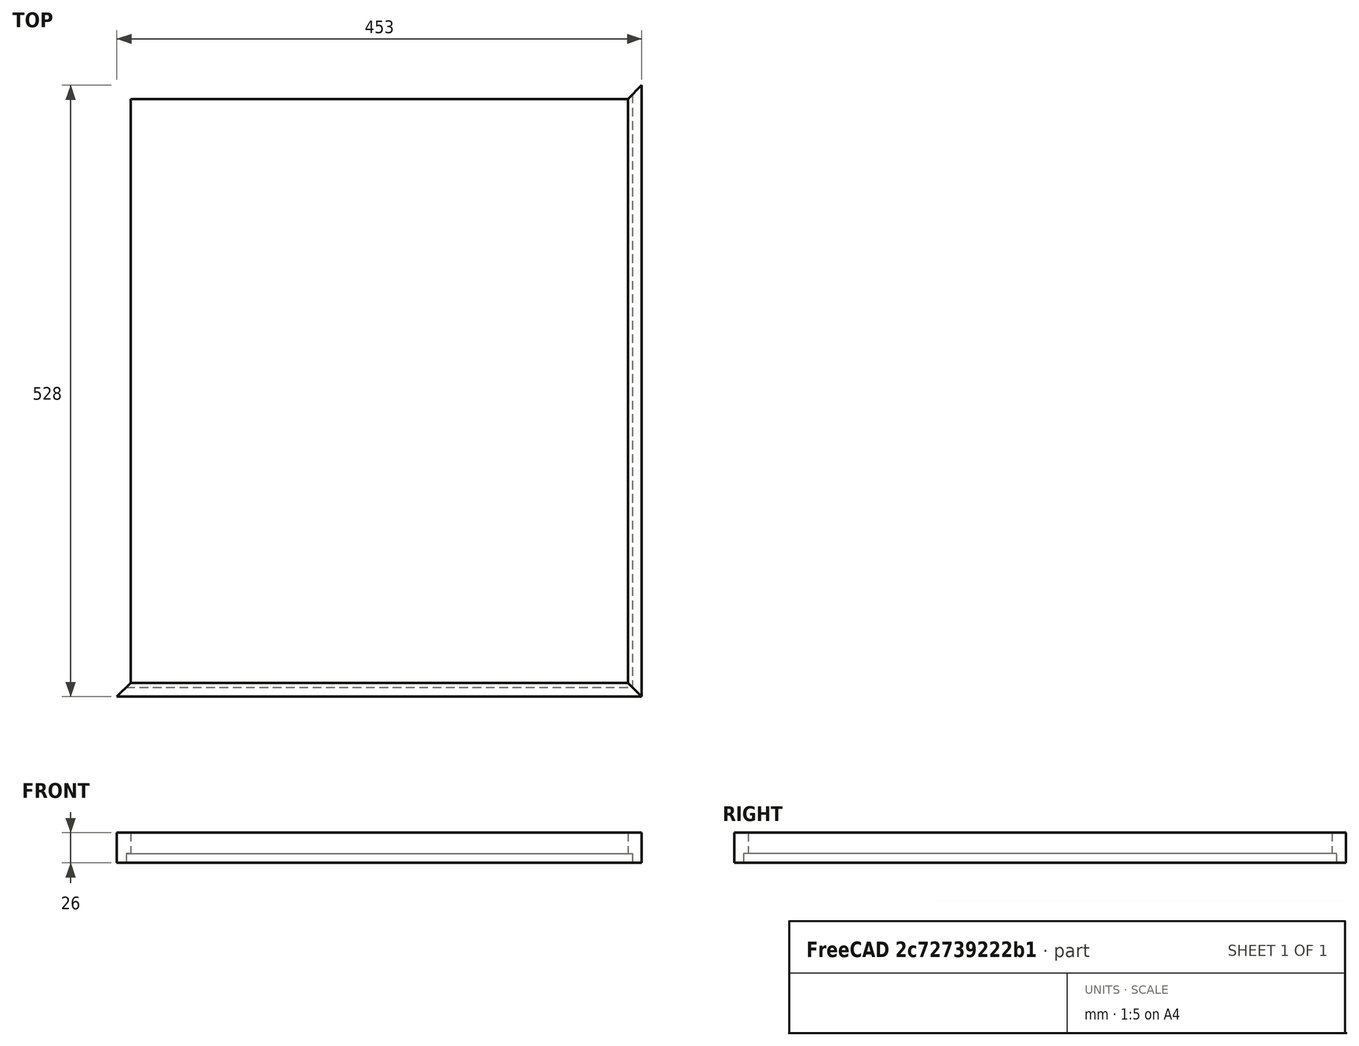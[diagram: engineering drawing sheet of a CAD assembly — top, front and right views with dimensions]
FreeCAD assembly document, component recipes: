
FREECAD ASSEMBLY — COMPONENT RECIPES ("streha")

This assembly document has 3 components, labeled P0..P2 below (a component is one placed body or linked part). 3 of them carry a construction recipe — the FreeCAD feature program that regenerates the part from scratch, quoted from this document or its linked companion documents; the rest are supplied as boundary geometry only. No exploded tour is included for this assembly.
COMPONENT P0 — recipe-attached ("slat_side", modeled in this document).
Construction recipe (the document's own serialized feature program — sketch geometry with constraints, then the solid features built on it; lengths are millimeters unless a unit is written):

FEATURE [PartDesign::CoordinateSystem] LCS_0005
  AttacherType = Attacher::AttachEngine3D
  MapMode = 2
  Support = -> [X_Axis006]
FEATURE [Sketcher::SketchObject] Sketch003  label="Sketch004"
  FullyConstrained = true
  MapMode = 5
  Placement = pos=(0,0,0) rot=(1,0,0;1.5708rad)
  Support = -> [XZ_Plane006]
  expr: Constraints[12] = Variables.inner_width / 2 + Variables.wall_thickness
  sketch-geometry (6):
    g0: LineSegment StartX=214.5 StartY=0 StartZ=0 EndX=218.5 EndY=0 EndZ=0
    g1: LineSegment StartX=218.5 StartY=0 StartZ=0 EndX=218.5 EndY=-8 EndZ=0
    g2: LineSegment StartX=218.5 StartY=-8 StartZ=0 EndX=226.5 EndY=-8 EndZ=0
    g3: LineSegment StartX=226.5 StartY=-8 StartZ=0 EndX=226.5 EndY=25.6324 EndZ=0
    g4: LineSegment StartX=214.5 StartY=30 StartZ=0 EndX=214.5 EndY=0 EndZ=0
    g5: LineSegment StartX=214.5 StartY=30 StartZ=0 EndX=226.5 EndY=25.6324 EndZ=0
  constraints (18):
    c: Horizontal(g0)
    c: Coincident(g0,g1)
    c: Vertical(g1)
    c: Coincident(g1,g2)
    c: Horizontal(g2)
    c: Coincident(g2,g3)
    c: Vertical(g3)
    c: Coincident(g4,g0)
    c: Vertical(g4)
    c: DistanceX(g0,g0) = 4  'c'
    c: DistanceY(g1,g1) = 8  'd'
    c: Horizontal(g0,g-1)
    c: DistanceX(g-1,g0) = 214.5
    c: DistanceX(g0,g2) = 12  'a'
    c: DistanceY(g4,g4) = 30  'b'
    c: Coincident(g5,g4)
    c: Coincident(g5,g3)
    c: Angle(g5) = -0.349066  'e'
FEATURE [PartDesign::Pad] Pad002
  Direction = (1,1,1)
  Length = 700
  Length2 = 100
  Midplane = true
  Placement = pos=(0,0,0) rot=(1,0,0;1.5708rad)
  Profile = -> Sketch003
  Type = 0
FEATURE [Sketcher::SketchObject] Sketch004  label="Sketch005"
  ExternalGeometry = -> [Pad002]
  FullyConstrained = true
  MapMode = 5
  Support = -> [XY_Plane006]
  expr: Constraints[14] = Variables.inner_depth + 2 * Variables.wall_thickness
  sketch-geometry (8):
    g0: LineSegment StartX=226.5 StartY=-350 StartZ=0 EndX=226.5 EndY=-264 EndZ=0
    g1: LineSegment StartX=226.5 StartY=-264 StartZ=0 EndX=214.5 EndY=-252 EndZ=0
    g2: LineSegment StartX=214.5 StartY=-252 StartZ=0 EndX=214.5 EndY=-350 EndZ=0
    g3: LineSegment StartX=226.5 StartY=350 StartZ=0 EndX=226.5 EndY=264 EndZ=0
    g4: LineSegment StartX=226.5 StartY=264 StartZ=0 EndX=214.5 EndY=252 EndZ=0
    g5: LineSegment StartX=214.5 StartY=252 StartZ=0 EndX=214.5 EndY=350 EndZ=0
    g6: LineSegment StartX=214.5 StartY=-350 StartZ=0 EndX=226.5 EndY=-350 EndZ=0
    g7: LineSegment StartX=214.5 StartY=350 StartZ=0 EndX=226.5 EndY=350 EndZ=0
  constraints (20):
    c: Coincident(g0,g-4)
    c: Coincident(g1,g0)
    c: Coincident(g2,g1)
    c: Coincident(g2,g-4)
    c: Vertical(g2)
    c: Vertical(g0)
    c: Coincident(g-3,g3)
    c: Vertical(g3)
    c: Coincident(g3,g4)
    c: Coincident(g4,g5)
    c: Coincident(g5,g-3)
    c: Vertical(g5)
    c: Equal(g4,g1)
    c: Equal(g5,g2)
    c: DistanceY(g1,g4) = 504
    c: Coincident(g6,g2)
    c: Coincident(g6,g0)
    c: Coincident(g7,g5)
    c: Coincident(g7,g3)
    c: Perpendicular(g4,g1)
FEATURE [PartDesign::Pocket] Pocket001
  BaseFeature = -> Pad002
  Length = 41
  Length2 = 100
  Midplane = true
  Placement = pos=(0,0,0) rot=(1,0,0;1.5708rad)
  Profile = -> Sketch004
  Type = 1
FEATURE [Sketcher::SketchObject] Sketch
  ExternalGeometry = -> [Pocket001]
  FullyConstrained = true
  MapMode = 5
  Placement = pos=(0,0,0) rot=(1,0,0;1.5708rad)
  Support = -> [XZ_Plane006]
  expr: Constraints[10] = Variables.bottom_thickness
  sketch-geometry (4):
    g0: LineSegment StartX=214.5 StartY=18 StartZ=0 EndX=226.5 EndY=18 EndZ=0
    g1: LineSegment StartX=226.5 StartY=18 StartZ=0 EndX=226.5 EndY=30 EndZ=0
    g2: LineSegment StartX=226.5 StartY=30 StartZ=0 EndX=214.5 EndY=30 EndZ=0
    g3: LineSegment StartX=214.5 StartY=30 StartZ=0 EndX=214.5 EndY=18 EndZ=0
  constraints (11):
    c: Coincident(g0,g1)
    c: Coincident(g1,g2)
    c: Coincident(g2,g3)
    c: Coincident(g3,g0)
    c: Horizontal(g0)
    c: Horizontal(g2)
    c: Vertical(g1)
    c: Vertical(g3)
    c: Coincident(g2,g-3)
    c: PointOnObject(g-3,g1)
    c: DistanceY(g-1,g0) = 18
FEATURE [PartDesign::Pocket] Pocket
  BaseFeature = -> Pocket001
  Length = 5
  Length2 = 100
  Midplane = true
  Placement = pos=(0,0,0) rot=(1,0,0;1.5708rad)
  Profile = -> Sketch
  Type = 1
FEATURE [PartDesign::Body] Body_3
  Group = -> [LCS_0005,Sketch003,Pad002,Sketch004,Pocket001,Sketch,Pocket]
  Origin = -> Origin006
  Tip = -> Pocket
COMPONENT P1 — recipe-attached ("slat_front_rear", modeled in this document).
Construction recipe (the document's own serialized feature program — sketch geometry with constraints, then the solid features built on it; lengths are millimeters unless a unit is written):

FEATURE [PartDesign::CoordinateSystem] LCS_0007
  AttacherType = Attacher::AttachEngine3D
  MapMode = 2
  Support = -> [X_Axis008]
FEATURE [Sketcher::SketchObject] Sketch005  label="Sketch006"
  FullyConstrained = true
  MapMode = 5
  Placement = pos=(0,0,0) rot=(0.57735,0.57735,0.57735;2.0944rad)
  Support = -> [YZ_Plane008]
  expr: Constraints[17] = Variables.inner_depth / 2 + Variables.wall_thickness
  sketch-geometry (6):
    g0: LineSegment StartX=-252 StartY=0 StartZ=0 EndX=-252 EndY=30 EndZ=0
    g1: LineSegment StartX=-264 StartY=25.6324 StartZ=0 EndX=-264 EndY=-8 EndZ=0
    g2: LineSegment StartX=-264 StartY=-8 StartZ=0 EndX=-256 EndY=-8 EndZ=0
    g3: LineSegment StartX=-256 StartY=-8 StartZ=0 EndX=-256 EndY=0 EndZ=0
    g4: LineSegment StartX=-256 StartY=0 StartZ=0 EndX=-252 EndY=0 EndZ=0
    g5: LineSegment StartX=-264 StartY=25.6324 StartZ=0 EndX=-252 EndY=30 EndZ=0
  constraints (18):
    c: Vertical(g0)
    c: Vertical(g1)
    c: Coincident(g1,g2)
    c: Horizontal(g2)
    c: Coincident(g2,g3)
    c: Vertical(g3)
    c: Coincident(g3,g4)
    c: Coincident(g4,g0)
    c: Horizontal(g4)
    c: Horizontal(g0,g-1)
    c: DistanceX(g4,g4) = 4
    c: DistanceY(g3,g3) = 8
    c: DistanceX(g1,g0) = 12
    c: DistanceY(g0,g0) = 30
    c: Coincident(g5,g1)
    c: Coincident(g5,g0)
    c: Angle(g5) = 0.349066
    c: DistanceX(g0,g-1) = 252
FEATURE [PartDesign::Pad] Pad003
  Direction = (1,1,1)
  Length = 700
  Length2 = 100
  Midplane = true
  Placement = pos=(0,0,0) rot=(0.57735,0.57735,0.57735;2.0944rad)
  Profile = -> Sketch005
  Type = 0
FEATURE [Sketcher::SketchObject] Sketch006  label="Sketch007"
  ExternalGeometry = -> [Pad003]
  FullyConstrained = true
  MapMode = 5
  Support = -> [XY_Plane008]
  expr: Constraints[19] = Variables.inner_width + 2 * Variables.wall_thickness
  sketch-geometry (8):
    g0: LineSegment StartX=-350 StartY=-264 StartZ=0 EndX=-350 EndY=-252 EndZ=0
    g1: LineSegment StartX=-350 StartY=-252 StartZ=0 EndX=-214.5 EndY=-252 EndZ=0
    g2: LineSegment StartX=-214.5 StartY=-252 StartZ=0 EndX=-226.5 EndY=-264 EndZ=0
    g3: LineSegment StartX=-226.5 StartY=-264 StartZ=0 EndX=-350 EndY=-264 EndZ=0
    g4: LineSegment StartX=350 StartY=-264 StartZ=0 EndX=350 EndY=-252 EndZ=0
    g5: LineSegment StartX=350 StartY=-252 StartZ=0 EndX=214.5 EndY=-252 EndZ=0
    g6: LineSegment StartX=214.5 StartY=-252 StartZ=0 EndX=226.5 EndY=-264 EndZ=0
    g7: LineSegment StartX=226.5 StartY=-264 StartZ=0 EndX=350 EndY=-264 EndZ=0
  constraints (20):
    c: Coincident(g-3,g0)
    c: Coincident(g0,g-3)
    c: Coincident(g0,g1)
    c: Coincident(g1,g2)
    c: Coincident(g2,g3)
    c: Coincident(g3,g0)
    c: Coincident(g-4,g4)
    c: Coincident(g4,g-4)
    c: Coincident(g4,g5)
    c: Coincident(g5,g6)
    c: Coincident(g6,g7)
    c: Coincident(g7,g4)
    c: Perpendicular(g2,g6)
    c: Equal(g2,g6)
    c: Equal(g1,g5)
    c: Horizontal(g1)
    c: Horizontal(g3)
    c: Horizontal(g7)
    c: Horizontal(g5)
    c: DistanceX(g1,g5) = 429
FEATURE [PartDesign::Pocket] Pocket002
  BaseFeature = -> Pad003
  Length = 5
  Length2 = 100
  Midplane = true
  Placement = pos=(0,0,0) rot=(0.57735,0.57735,0.57735;2.0944rad)
  Profile = -> Sketch006
  Type = 1
FEATURE [Sketcher::SketchObject] Sketch008  label="Sketch009"
  ExternalGeometry = -> [Pocket002]
  FullyConstrained = true
  MapMode = 5
  Placement = pos=(0,0,0) rot=(0.57735,0.57735,0.57735;2.0944rad)
  Support = -> [YZ_Plane008]
  expr: Constraints[10] = Variables.bottom_thickness
  sketch-geometry (4):
    g0: LineSegment StartX=-264 StartY=30 StartZ=0 EndX=-252 EndY=30 EndZ=0
    g1: LineSegment StartX=-252 StartY=30 StartZ=0 EndX=-252 EndY=18 EndZ=0
    g2: LineSegment StartX=-252 StartY=18 StartZ=0 EndX=-264 EndY=18 EndZ=0
    g3: LineSegment StartX=-264 StartY=18 StartZ=0 EndX=-264 EndY=30 EndZ=0
  constraints (11):
    c: Coincident(g0,g1)
    c: Coincident(g1,g2)
    c: Coincident(g2,g3)
    c: Coincident(g3,g0)
    c: Horizontal(g0)
    c: Horizontal(g2)
    c: Vertical(g1)
    c: Vertical(g3)
    c: Coincident(g0,g-3)
    c: PointOnObject(g-3,g3)
    c: DistanceY(g-1,g1) = 18
FEATURE [PartDesign::Pocket] Pocket003
  BaseFeature = -> Pocket002
  Length = 5
  Length2 = 100
  Midplane = true
  Placement = pos=(0,0,0) rot=(0.57735,0.57735,0.57735;2.0944rad)
  Profile = -> Sketch008
  Type = 1
FEATURE [PartDesign::Body] Body_4
  Group = -> [LCS_0007,Sketch005,Pad003,Sketch006,Pocket002,Sketch008,Pocket003]
  Origin = -> Origin008
  Tip = -> Pocket003
COMPONENT P2 — recipe-attached ("bottom", modeled in this document).
Construction recipe (the document's own serialized feature program — sketch geometry with constraints, then the solid features built on it; lengths are millimeters unless a unit is written):

FEATURE [PartDesign::CoordinateSystem] LCS_0011
  AttacherType = Attacher::AttachEngine3D
  MapMode = 2
  Support = -> [X_Axis012]
FEATURE [Sketcher::SketchObject] Sketch007  label="Sketch008"
  FullyConstrained = true
  MapMode = 5
  Support = -> [XY_Plane012]
  expr: Constraints[12] = Variables.inner_depth + Variables.wall_thickness * 2
  expr: Constraints[11] = Variables.inner_width + Variables.wall_thickness * 2
  sketch-geometry (5):
    g0: LineSegment StartX=214.5 StartY=252 StartZ=0 EndX=-214.5 EndY=252 EndZ=0
    g1: LineSegment StartX=-214.5 StartY=252 StartZ=0 EndX=-214.5 EndY=-252 EndZ=0
    g2: LineSegment StartX=-214.5 StartY=-252 StartZ=0 EndX=214.5 EndY=-252 EndZ=0
    g3: LineSegment StartX=214.5 StartY=-252 StartZ=0 EndX=214.5 EndY=252 EndZ=0
    g4: Circle CenterX=0 CenterY=0 CenterZ=0 NormalX=0 NormalY=0 NormalZ=1 AngleXU=0 Radius=330.929
  constraints (14):
    c: Coincident(g0,g1)
    c: Coincident(g1,g2)
    c: Coincident(g2,g3)
    c: Coincident(g3,g0)
    c: Equal(g0,g2)
    c: PointOnObject(g0,g4)
    c: PointOnObject(g1,g4)
    c: PointOnObject(g2,g4)
    c: PointOnObject(g3,g4)
    c: Coincident(g4,g-1)
    c: Horizontal(g2)
    c: DistanceX(g0,g0) = 429
    c: DistanceY(g3,g3) = 504
    c: Vertical(g1)
FEATURE [PartDesign::Pad] Pad004
  Direction = (1,1,1)
  Length = 18
  Length2 = 100
  Profile = -> Sketch007
  Type = 0
  expr: Length = Variables.bottom_thickness
FEATURE [Sketcher::SketchObject] Sketch009  label="Sketch010"
  FullyConstrained = true
  MapMode = 5
  Support = -> [XY_Plane012]
  expr: Constraints[9] = Variables.inner_depth
  expr: Constraints[8] = Variables.inner_width
  sketch-geometry (4):
    g0: LineSegment StartX=-187.5 StartY=-225 StartZ=0 EndX=187.5 EndY=-225 EndZ=0
    g1: LineSegment StartX=187.5 StartY=-225 StartZ=0 EndX=187.5 EndY=225 EndZ=0
    g2: LineSegment StartX=187.5 StartY=225 StartZ=0 EndX=-187.5 EndY=225 EndZ=0
    g3: LineSegment StartX=-187.5 StartY=225 StartZ=0 EndX=-187.5 EndY=-225 EndZ=0
  constraints (10):
    c: Coincident(g0,g1)
    c: Coincident(g1,g2)
    c: Coincident(g2,g3)
    c: Coincident(g3,g0)
    c: Horizontal(g2)
    c: Vertical(g3)
    c: Symmetric(g0,g0,g-2)
    c: Symmetric(g0,g1,g-1)
    c: DistanceX(g2,g2) = 375
    c: DistanceY(g3,g3) = 450
FEATURE [PartDesign::Body] Body_5
  Group = -> [LCS_0011,Sketch007,Pad004,Sketch009]
  Origin = -> Origin012
  Tip = -> Pad004
PROVENANCE & LICENSES
A FreeCAD (.FCStd) document from a public repository crawl; recipes are the document's own serialized feature recipes (and, for linked parts, companion documents' recipes).
License: apache-2.0.
